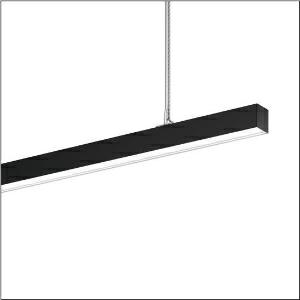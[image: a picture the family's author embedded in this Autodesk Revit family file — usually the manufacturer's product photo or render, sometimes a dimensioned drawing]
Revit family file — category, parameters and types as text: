
# Revit family: silica_r__21_51mx30da34bb_31c6
name_source: partatom
category: Lighting Fixtures
units: mm (PartAtom-declared; Revit-internal decimal feet)

## family parameters
Cut with Voids When Loaded = No
Host = Face
Light Source = No
Part Type = Normal
Room Calculation Point = No
Round Connector Dimension = Use Diameter
Shared = No

## types (1)
- --- (1 x LED, 4210 lm, 27.7 W, 3000K)
    Apparent Load = 28 VA
    CIE Flux Codes = 47 79 96 57 100
    Color Rendering = 80
    Color Temperature = 3000K
    Default Elevation = 1800 mm
    Description = Silica® 21, office luminaire, primary optical cover: cover, of PMMA, opal, light emission: direct/indirect distribution, primary light characteristic: symmetric, installation type: suspended mounting, LED, rated luminous flux: 4.210lm, luminous efficacy: 152lm/W, light colour: 830, colour temperature: 3000K, with terminal, 3+2-pole, max. 2.5mm², mains connection: 220..240V, AC, 50/60Hz, rated input power: 27.7W, luminaire housing, of aluminium, jet black (RAL 9005), length: 1.204mm, width: 53mm, height: 53mm, protection rating (complete): IP20, insulation class (complete): insulation class I (protective earthing), certification: CE, permissible operating ambient temperature: 0..+35°C, standard: EN 50419, packaging unit: 1 piece
    Height = 53 mm
    Lamp = 1 x LED
    Lamp Light Flux = 4210 lm
    Lamp Power = 27.7 W
    Lamp count = 1
    Length = 1204 mm
    Luminous efficacy = 152 lm/W
    Manufacturer = Siteco
    ModVariant = No
    Model = 51MX30DA34BB
    Mounting Place = Ceiling
    Mounting Type = Pendant
    Number of Poles = 1
    OnlyDefault = Yes
    Power Factor = 1
    Product Name = Silica® 21
    Product group = office luminaire | ceiling pendant
    ProductGroupID = 902
    Protection Class = Protection class I
    Protection Degree = IP 20
    RLX_Detail_Level = 1
    RLX_Emergency_Light_Flux = 0 lm
    RLX_Emergency_Type = 0
    RLX_Emergency_Type_DB = No
    RlxData = <blob elided: 25945 chars, md5=b88e451b>
    Socket = socket
    Standby Power = 0 W
    System Light Flux = 4210 lm
    System Power = 28 W
    Type Comments = factory setting: luminous flux: 100 % | dim-lin: 254 | 233 mA
    Type Image = l_1297744.jpg
    URL = http://relux.com
    VarID = @adj_047349
    Voltage = 0 V
    Weight = 0.00 kg
    Width = 53 mm

## geometry (parser evidence)
native form markers: Blend x4, Sweep x12
no freeform markers — native parametric forms only
